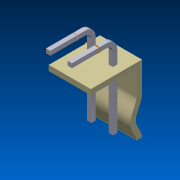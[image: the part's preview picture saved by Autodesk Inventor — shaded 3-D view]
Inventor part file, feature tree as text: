
AUTODESK INVENTOR PART (.ipt)
format: ipt  version: 2015 SP1 (Build 190203100, 203)  size: 157,184 bytes
history: native  units: mm
features: sketch x4, other x3, sweep x2, projected_geometry x2
ambient origin geometry x8: Origin, YZ Plane, XZ Plane, XY Plane, X Axis, Y Axis, Z Axis, Center Point
bodies: Body1 (feature_tree)
feature tree (11):
  other  "Твердое тело1"
  sketch  "Эскиз1"
  other  "РабПлоскость1"
  other  "РабПлоскость2"
  sweep  "Сдвиг1"
  sweep  "Сдвиг2"
  sketch  "Эскиз4"
  sketch  "Эскиз2"
  sketch  "Эскиз3"
  projected_geometry  "Спроецированная петля1"
  projected_geometry  "Спроецированная петля2"
